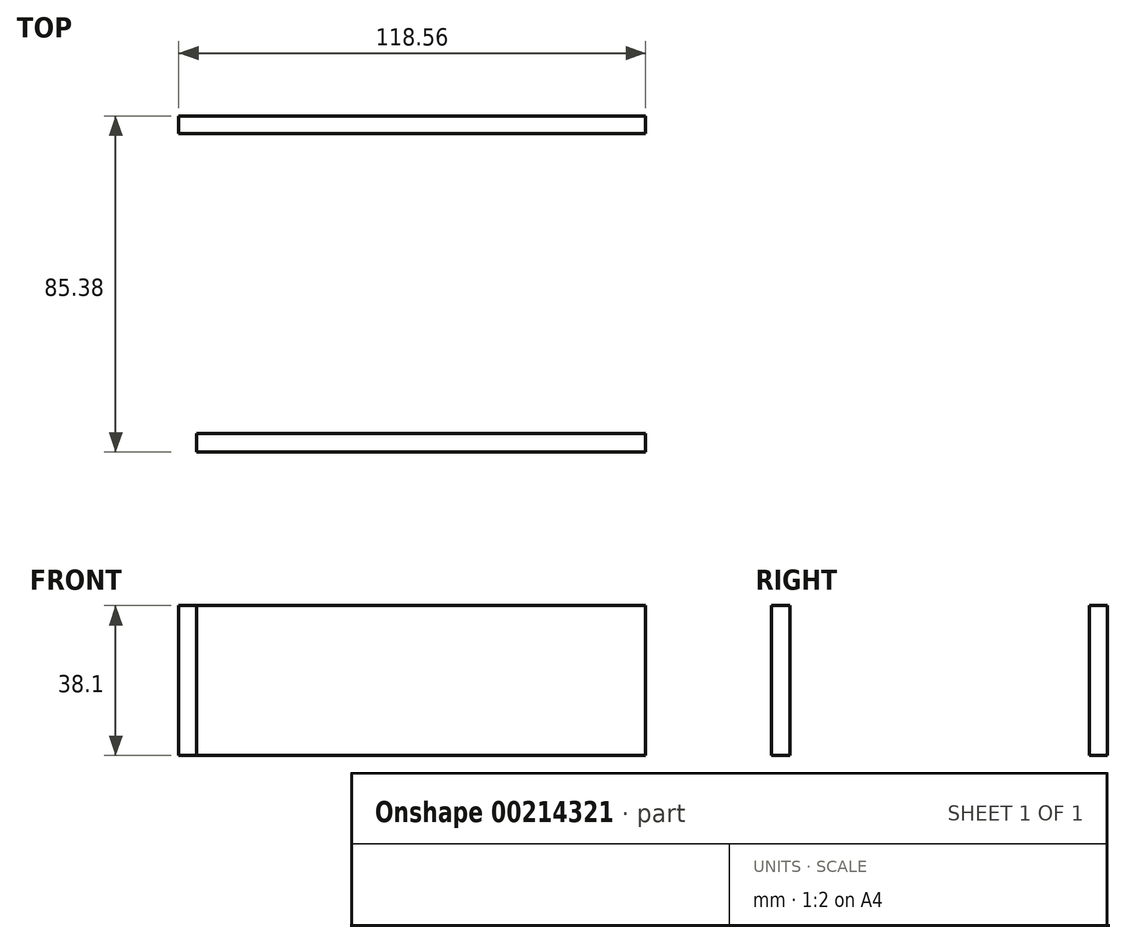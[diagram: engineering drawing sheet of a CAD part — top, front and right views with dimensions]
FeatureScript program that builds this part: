
annotation { "Feature Type Name" : "Feature", "Feature Type Description" : "" }
export const myFeature = defineFeature(function(context is Context, id is Id, definition is map)
    precondition{}
    {
        {
            var Q0;
            Q0=qCreatedBy(makeId("Top.planeOp"),FACE);
            var sketch = newSketch(context, id + "F0", { "sketchPlane" : qUnion([Q0])});
            skLineSegment(sketch, "E0.bottom", {"start": v(-54.85, 43.82) * mm, "end": v(63.7, 43.82) * mm});
            skLineSegment(sketch, "E0.top", {"start": v(-54.85, 39.3) * mm, "end": v(63.7, 39.3) * mm});
            skLineSegment(sketch, "E0.left", {"start": v(-54.85, 43.82) * mm, "end": v(-54.85, 39.3) * mm});
            skLineSegment(sketch, "E0.right", {"start": v(63.7, 43.82) * mm, "end": v(63.7, 39.3) * mm});
            skLineSegment(sketch, "E1.bottom", {"start": v(-54.85, 39.3) * mm, "end": v(-50.32, 39.3) * mm});
            skLineSegment(sketch, "E1.top", {"start": v(-54.85, -41.56) * mm, "end": v(-50.32, -41.56) * mm});
            skLineSegment(sketch, "E1.left", {"start": v(-54.85, 39.3) * mm, "end": v(-54.85, -41.56) * mm});
            skLineSegment(sketch, "E1.right", {"start": v(-50.32, 39.3) * mm, "end": v(-50.32, -41.56) * mm});
            skLineSegment(sketch, "E2.bottom", {"start": v(-50.32, -41.56) * mm, "end": v(63.7, -41.56) * mm});
            skLineSegment(sketch, "E2.top", {"start": v(-50.32, -36.85) * mm, "end": v(63.7, -36.85) * mm});
            skLineSegment(sketch, "E2.left", {"start": v(-50.32, -41.56) * mm, "end": v(-50.32, -36.85) * mm});
            skLineSegment(sketch, "E2.right", {"start": v(63.7, -41.56) * mm, "end": v(63.7, -36.85) * mm});
            skLineSegment(sketch, "E3.bottom", {"start": v(63.7, -36.85) * mm, "end": v(60.13, -36.85) * mm});
            skLineSegment(sketch, "E3.top", {"start": v(63.7, 39.3) * mm, "end": v(60.13, 39.3) * mm});
            skLineSegment(sketch, "E3.left", {"start": v(63.7, -36.85) * mm, "end": v(63.7, 39.3) * mm});
            skLineSegment(sketch, "E3.right", {"start": v(60.13, -36.85) * mm, "end": v(60.13, 39.3) * mm});
            skLineSegment(sketch, "E4.bottom", {"start": v(4.43, 39.3) * mm, "end": v(0, 39.3) * mm});
            skLineSegment(sketch, "E4.top", {"start": v(4.43, -36.85) * mm, "end": v(0, -36.85) * mm});
            skLineSegment(sketch, "E4.left", {"start": v(4.43, 39.3) * mm, "end": v(4.43, -36.85) * mm});
            skLineSegment(sketch, "E4.right", {"start": v(0, 39.3) * mm, "end": v(0, -36.85) * mm});
            skSolve(sketch);
        }
        {
            var Q0;
            Q0=makeQuery(id+"F0.imprint","IMPRINT",FACE,{"disambiguationData":[TD([[makeQuery(id+"F0.imprint","IMPRINT",EDGE,{"derivedFrom":sQuery(id+"F0.wireOp",EDGE,"E1.bottom")}),-1.0]])]});
            var Q1;
            Q1=makeQuery(id+"F0.imprint","IMPRINT",FACE,{"disambiguationData":[TD([[makeQuery(id+"F0.imprint","IMPRINT",EDGE,{"derivedFrom":sQuery(id+"F0.wireOp",EDGE,"E3.bottom")}),-1.0]])]});
            var Q2;
            Q2=makeQuery(id+"F0.imprint","IMPRINT",FACE,{"disambiguationData":[TD([[makeQuery(id+"F0.imprint","IMPRINT",EDGE,{"derivedFrom":sQuery(id+"F0.wireOp",EDGE,"E2.bottom")}),1.0]])]});
            var Q3;
            Q3=makeQuery(id+"F0.imprint","IMPRINT",FACE,{"disambiguationData":[TD([[makeQuery(id+"F0.imprint","IMPRINT",EDGE,{"derivedFrom":sQuery(id+"F0.wireOp",EDGE,"E4.bottom")}),1.0]])]});
            var Q4;
            Q4=makeQuery(id+"F0.imprint","IMPRINT",FACE,{"disambiguationData":[TD([[makeQuery(id+"F0.imprint","IMPRINT",EDGE,{"derivedFrom":sQuery(id+"F0.wireOp",EDGE,"E0.bottom")}),-1.0]])]});
            extrude(context, id + "F1", {"entities" : qUnion([Q0, Q1, Q2, Q3, Q4]), "depth" : 38.1 * mm});
        }
    });
